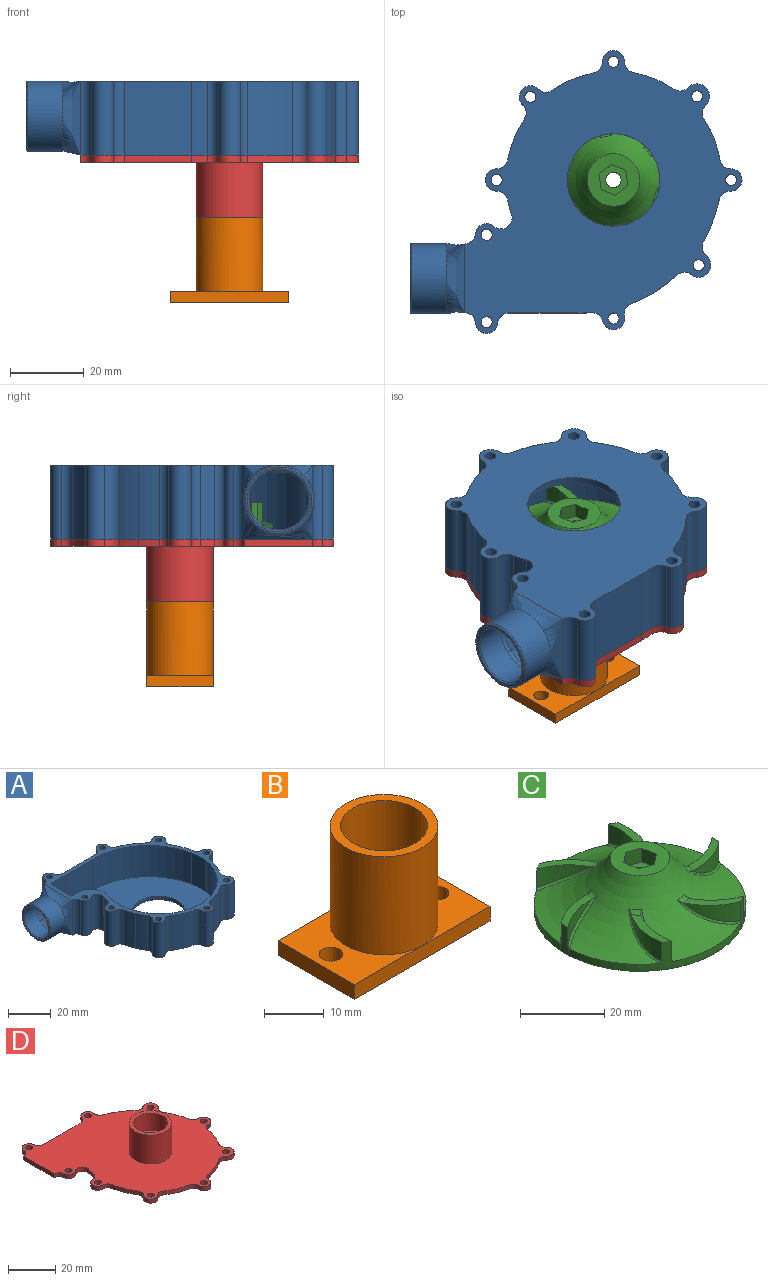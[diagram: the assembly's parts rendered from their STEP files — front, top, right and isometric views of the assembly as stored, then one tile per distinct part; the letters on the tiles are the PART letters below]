
ASSEMBLY  parts=4 mates=3
PART A: 83 faces, bbox 89.8x76.4x20.8 mm
  f0: cylinder r=29.1mm len=20mm, axis (0,0,-1), area 123.2mm2, adj f1,f7,f16,f63
  f1: cylinder r=29.1mm len=20mm, axis (0,0,-1), area 116.2mm2, adj f0,f7,f16,f54
  f2: cylinder r=29.1mm len=20mm, axis (0,0,-1), area 242.2mm2, adj f7,f16,f50,f56
  f3: cylinder r=29.1mm len=20mm, axis (0,0,-1), area 236.9mm2, adj f7,f16,f46,f52
  f4: cylinder r=38.12mm len=20mm, axis (0,0,-1), area 241.8mm2, adj f7,f11,f16,f40
  f5: cylinder r=38.12mm len=20mm, axis (0,0,-1), area 292.6mm2, adj f7,f16,f36,f42
  f6: cylinder r=8.51mm len=18mm, axis (0,0,-1), area 233.2mm2, adj f7,f26,f27,f28,f29,f30
  f7: plane 76.42x75.05mm, normal (0,0,1), area 691.8mm2, adj f0,f1,f2,f3,f4,f5,f6,f8
  f8: cylinder r=29.1mm len=20mm, axis (0,0,-1), area 80mm2, adj f7,f15,f16,f61
  f9: cylinder r=29.1mm len=20mm, axis (0,0,-1), area 235.3mm2, adj f7,f10,f16,f48
  f10: cylinder r=3mm len=20mm, axis (0,0,-1), area 83.6mm2, adj f7,f9,f16,f44
  f11: cylinder r=3mm len=20mm, axis (0,0,-1), area 84.8mm2, adj f4,f7,f16,f44
  f12: cylinder r=38.12mm len=20mm, axis (0,0,-1), area 85.1mm2, adj f7,f13,f16,f38
  f13: plane 20x18.02mm, normal (0,1,0), area 360.4mm2, adj f7,f12,f16,f33
  f14: plane 20x0.02mm, normal (0,-1,0), area 0.4mm2, adj f7,f16,f58,f66
  f15: cylinder r=3mm len=20mm, axis (0,0,-1), area 156mm2, adj f7,f8,f16,f59
  f16: plane 76.42x75.05mm, normal (0,0,-1), area 3092.9mm2, adj f0,f1,f2,f3,f4,f5,f8,f9
  f17: cylinder r=27.1mm len=19.22mm, axis (0,0,-1), area 354mm2, adj f7,f18,f27,f28
  f18: cylinder r=27.1mm len=51.79mm, axis (0,0,-1), area 1258.4mm2, adj f7,f17,f19,f28
  f19: cylinder r=5mm len=18mm, axis (0,0,-1), area 0.8mm2, adj f7,f18,f20,f28
  f20: cylinder r=24.78mm len=18mm, axis (0,0,-1), area 178.9mm2, adj f7,f19,f21,f28
  f21: cylinder r=5mm len=18mm, axis (0,0,-1), area 3.9mm2, adj f7,f20,f22,f28
  f22: cylinder r=36.12mm len=36.86mm, axis (0,0,-1), area 918mm2, adj f7,f21,f23,f28
  f23: plane 18.05x18mm, normal (0,-1,0), area 324.9mm2, adj f7,f22,f24,f28
  f24: plane 18x9.91mm, normal (0.01,-1,0), area 178.4mm2, adj f7,f23,f25,f28
  f25: plane 18x14.36mm, normal (1,0,0), area 29.1mm2, adj f7,f24,f26,f28,f30,f31
  f26: plane 3.82x2mm, normal (-0.08,1,0), area 7.7mm2, adj f6,f7,f25,f30
  f27: cylinder r=5mm len=18mm, axis (0,0,-1), area 7.9mm2, adj f6,f7,f17,f28
  f28: plane 67.53x61.45mm, normal (0,0,1), area 2433mm2, adj f6,f17,f18,f19,f20,f21,f22,f23
  f29: plane 16x9.59mm, normal (0,1,0), area 153.4mm2, adj f6,f28,f30,f73
  f30: plane 14.56x9.59mm, normal (0,0,-1), area 31.9mm2, adj f6,f25,f26,f29,f31,f72
  f31: plane 16x2mm, normal (0,-1,0), area 32mm2, adj f25,f28,f30,f71
  f32: cylinder r=3mm len=20mm, axis (0,0,-1), area 88.8mm2, adj f7,f16,f34,f68
  f33: cylinder r=3mm len=20mm, axis (0,0,-1), area 89.2mm2, adj f7,f13,f16,f34
  f34: cylinder r=3mm len=20mm, axis (0,0,-1), area 179.5mm2, adj f7,f16,f32,f33
  f35: cylinder r=1.5mm len=20mm, axis (0,0,-1), area 188.5mm2, adj f7,f16
  f36: cylinder r=3mm len=20mm, axis (0,0,-1), area 84.2mm2, adj f5,f7,f16,f37
  f37: cylinder r=3mm len=20mm, axis (0,0,-1), area 186mm2, adj f7,f16,f36,f38
  f38: cylinder r=3mm len=20mm, axis (0,0,-1), area 84.2mm2, adj f7,f12,f16,f37
  f39: cylinder r=1.5mm len=20mm, axis (0,0,-1), area 188.5mm2, adj f7,f16
  f40: cylinder r=3mm len=20mm, axis (0,0,-1), area 84.7mm2, adj f4,f7,f16,f41
  f41: cylinder r=3.26mm len=20mm, axis (0,0,-1), area 203.7mm2, adj f7,f16,f40,f42
  f42: cylinder r=3mm len=20mm, axis (0,0,-1), area 84.7mm2, adj f5,f7,f16,f41
  f43: cylinder r=1.5mm len=20mm, axis (0,0,-1), area 188.5mm2, adj f7,f16
  f44: cylinder r=3mm len=20mm, axis (0,0,-1), area 191mm2, adj f7,f10,f11,f16
  f45: cylinder r=1.5mm len=20mm, axis (0,0,-1), area 188.5mm2, adj f7,f16
  f46: cylinder r=3mm len=20mm, axis (0,0,-1), area 83.6mm2, adj f3,f7,f16,f47
  f47: cylinder r=3.38mm len=20mm, axis (0,0,-1), area 215.1mm2, adj f7,f16,f46,f48
  f48: cylinder r=3mm len=20mm, axis (0,0,-1), area 83.6mm2, adj f7,f9,f16,f47
  f49: cylinder r=1.5mm len=20mm, axis (0,0,-1), area 188.5mm2, adj f7,f16
  f50: cylinder r=3mm len=20mm, axis (0,0,-1), area 83.6mm2, adj f2,f7,f16,f51
  f51: cylinder r=3mm len=20mm, axis (0,0,-1), area 189.8mm2, adj f7,f16,f50,f52
  f52: cylinder r=3mm len=20mm, axis (0,0,-1), area 83.6mm2, adj f3,f7,f16,f51
  f53: cylinder r=1.5mm len=20mm, axis (0,0,-1), area 188.5mm2, adj f7,f16
  f54: cylinder r=3mm len=20mm, axis (0,0,-1), area 83.6mm2, adj f1,f7,f16,f55
  f55: cylinder r=3mm len=20mm, axis (0,0,-1), area 189.8mm2, adj f7,f16,f54,f56
  f56: cylinder r=3mm len=20mm, axis (0,0,-1), area 83.6mm2, adj f2,f7,f16,f55
  f57: cylinder r=1.5mm len=20mm, axis (0,0,-1), area 188.5mm2, adj f7,f16
  f58: cylinder r=3mm len=20mm, axis (0,0,-1), area 89.2mm2, adj f7,f14,f16,f59
  f59: cylinder r=3mm len=20mm, axis (0,0,-1), area 131.5mm2, adj f7,f15,f16,f58
  f60: cylinder r=1.5mm len=20mm, axis (0,0,-1), area 188.5mm2, adj f7,f16
  f61: cylinder r=3mm len=20mm, axis (0,0,-1), area 83.6mm2, adj f7,f8,f16,f62
  f62: cylinder r=3mm len=20mm, axis (0,0,-1), area 189.8mm2, adj f7,f16,f61,f63
  f63: cylinder r=3mm len=20mm, axis (0,0,-1), area 83.6mm2, adj f0,f7,f16,f62
  f64: cylinder r=1.5mm len=20mm, axis (0,0,-1), area 188.5mm2, adj f7,f16
  f65: cylinder r=12.5mm len=25mm, axis (0,0,-1), area 157.1mm2, adj f16,f28
  f66: bspline ~20x4.7mm, area 84.7mm2, adj f14,f67,f69,f74
  f67: bspline ~18.52x4.79mm, area 86.6mm2, adj f7,f66,f68,f74
  f68: bspline ~20x4.79mm, area 85.6mm2, adj f32,f67,f69,f74
  f69: bspline ~18.52x4.79mm, area 81.8mm2, adj f16,f66,f68,f74
  f70: bspline ~14.52x4.78mm, area 65.1mm2, adj f28,f71,f73,f79
  f71: bspline ~16x4.78mm, area 69.3mm2, adj f31,f70,f72,f80
  f72: bspline ~14.52x4.78mm, area 66.7mm2, adj f30,f71,f73,f78
  f73: bspline ~16x4.71mm, area 68.3mm2, adj f29,f70,f72,f77
  f74: cylinder r=9.5mm len=19mm, axis (1,0,0), area 567.1mm2, adj f66,f67,f68,f69,f82
  f75: plane 18x18mm, normal (-1,0,0), area 27.5mm2, adj f81,f82
  f76: cylinder r=8mm len=16mm, axis (-1,0,0), area 399mm2, adj f77,f78,f79,f80,f81
  f77: bspline ~12.11x2.96mm, area 20.1mm2, adj f73,f76,f78,f79
  f78: bspline ~12.11x2.96mm, area 20.2mm2, adj f72,f76,f77,f80
  f79: bspline ~12.11x2.96mm, area 20.2mm2, adj f70,f76,f77,f80
  f80: bspline ~12.11x2.96mm, area 20.2mm2, adj f71,f76,f78,f79
  f81: torus R=8.5mm, axis (1,0,0), area 40.4mm2, adj f75,f76
  f82: torus R=9mm, axis (1,0,0), area 46mm2, adj f74,f75
PART B: 12 faces, bbox 32x18x23 mm
  f0: cylinder r=7.25mm len=23mm, axis (0,0,-1), area 1047.7mm2, adj f2,f9
  f1: cylinder r=9mm len=20mm, axis (0,0,-1), area 1131mm2, adj f2,f3,f6
  f2: plane 18x18mm, normal (0,0,1), area 89.3mm2, adj f0,f1
  f3: plane 18x16mm, normal (0,0,1), area 148.2mm2, adj f1,f5,f7,f8,f11
  f4: plane 18x3mm, normal (-1,0,0), area 54mm2, adj f6,f7,f8,f9
  f5: plane 18x3mm, normal (1,0,0), area 54mm2, adj f3,f7,f8,f9
  f6: plane 18x16mm, normal (0,0,1), area 148.2mm2, adj f1,f4,f7,f8,f10
  f7: plane 32x3mm, normal (0,1,0), area 96mm2, adj f3,f4,f5,f6,f9
  f8: plane 32x3mm, normal (0,-1,0), area 96mm2, adj f3,f4,f5,f6,f9
  f9: plane 32x18mm, normal (0,0,-1), area 385.7mm2, adj f0,f4,f5,f7,f8,f10,f11
  f10: cylinder r=2mm len=4mm, axis (0,0,-1), area 37.7mm2, adj f6,f9
  f11: cylinder r=2mm len=4mm, axis (0,0,-1), area 37.7mm2, adj f3,f9
PART C: 48 faces, bbox 61.1x61.1x26.7 mm
  f0: cylinder r=2.1mm len=11mm, axis (0,0,-1), area 145.1mm2, adj f3,f29
  f1: torus R=29.21mm, axis (0,0,-1), area 1865.6mm2, adj f2,f4,f30,f31,f32,f33,f34,f35
  f2: plane 14.2x14.2mm, normal (0,0,1), area 112.2mm2, adj f1,f23,f24,f25,f26,f27,f28
  f3: plane 50.2x50.2mm, normal (0,0,-1), area 1965.4mm2, adj f0,f4
  f4: cylinder r=25.1mm len=50.2mm, axis (0,0,-1), area 400.2mm2, adj f1,f3,f5,f6,f7,f8,f9,f10
  f5: cylinder r=18mm len=12.05mm, axis (0,0,-1), area 35.5mm2, adj f4,f7,f39
  f6: cylinder r=18mm len=13.06mm, axis (0,0,-1), area 49.9mm2, adj f4,f7,f38,f46
  f7: plane 12.88x6.41mm, normal (0,0,1), area 27.6mm2, adj f4,f5,f6,f39,f46
  f8: plane 14.32x4.63mm, normal (0,0,1), area 27.6mm2, adj f4,f9,f10,f37,f45
  f9: cylinder r=18mm len=13.33mm, axis (0,0,-1), area 49.9mm2, adj f4,f8,f36,f45
  f10: cylinder r=18mm len=12.56mm, axis (0,0,-1), area 35.5mm2, adj f4,f8,f37
  f11: plane 12.88x6.41mm, normal (0,0,1), area 27.6mm2, adj f4,f12,f13,f33,f43
  f12: cylinder r=18mm len=12.05mm, axis (0,0,-1), area 35.5mm2, adj f4,f11,f33
  f13: cylinder r=18mm len=13.06mm, axis (0,0,-1), area 49.9mm2, adj f4,f11,f32,f43
  f14: cylinder r=18mm len=13.33mm, axis (0,0,-1), area 49.9mm2, adj f4,f16,f30,f42
  f15: cylinder r=18mm len=12.56mm, axis (0,0,-1), area 35.5mm2, adj f4,f16,f31
  f16: plane 14.32x4.63mm, normal (0,0,1), area 27.6mm2, adj f4,f14,f15,f31,f42
  f17: cylinder r=18mm len=10.03mm, axis (0,0,-1), area 49.9mm2, adj f4,f19,f34,f44
  f18: cylinder r=18mm len=9.7mm, axis (0,0,-1), area 35.5mm2, adj f4,f19,f35
  f19: plane 11.94x9.52mm, normal (0,0,1), area 27.6mm2, adj f4,f17,f18,f35,f44
  f20: cylinder r=18mm len=9.7mm, axis (0,0,-1), area 35.5mm2, adj f4,f22,f40
  f21: cylinder r=18mm len=10.03mm, axis (0,0,-1), area 49.9mm2, adj f4,f22,f41,f47
  f22: plane 11.94x9.52mm, normal (0,0,1), area 27.6mm2, adj f4,f20,f21,f40,f47
  f23: plane 4x3.93mm, normal (0.36,0.93,0), area 16.9mm2, adj f2,f24,f28,f29
  f24: plane 4x3.28mm, normal (-0.63,0.78,0), area 16.9mm2, adj f2,f23,f25,f29
  f25: plane 4.16x4mm, normal (-0.99,-0.15,0), area 16.9mm2, adj f2,f24,f26,f29
  f26: plane 4x3.93mm, normal (-0.36,-0.93,0), area 16.9mm2, adj f2,f25,f27,f29
  f27: plane 4x3.28mm, normal (0.63,-0.78,0), area 16.9mm2, adj f2,f26,f28,f29
  f28: plane 4.16x4mm, normal (0.99,0.15,0), area 16.9mm2, adj f2,f23,f27,f29
  f29: plane 8.33x7.86mm, normal (0,0,1), area 32.3mm2, adj f0,f23,f24,f25,f26,f27,f28
  f30: bspline ~17.28x8.18mm, area 11mm2, adj f1,f4,f14,f42
  f31: bspline ~16.64x8.2mm, area 13.1mm2, adj f1,f4,f15,f16,f42
  f32: bspline ~16.34x8.08mm, area 11mm2, adj f1,f4,f13,f43
  f33: bspline ~16.1x8.2mm, area 13.1mm2, adj f1,f4,f11,f12,f43
  f34: bspline ~12.58x12.41mm, area 11mm2, adj f1,f4,f17,f44
  f35: bspline ~12.7x10.93mm, area 13.1mm2, adj f1,f4,f18,f19,f44
  f36: bspline ~17.28x8.18mm, area 11mm2, adj f1,f4,f9,f45
  f37: bspline ~16.64x8.2mm, area 13.1mm2, adj f1,f4,f8,f10,f45
  f38: bspline ~16.34x8.08mm, area 11mm2, adj f1,f4,f6,f46
  f39: bspline ~16.1x8.2mm, area 13.1mm2, adj f1,f4,f5,f7,f46
  f40: bspline ~12.7x10.93mm, area 13.1mm2, adj f1,f4,f20,f22,f47
  f41: bspline ~12.58x12.41mm, area 11mm2, adj f1,f4,f21,f47
  f42: torus R=13.36mm, axis (0,0,1), area 4mm2, adj f1,f14,f16,f30,f31
  f43: torus R=13.36mm, axis (0,0,1), area 4mm2, adj f1,f11,f13,f32,f33
  f44: torus R=13.36mm, axis (0,0,1), area 4mm2, adj f1,f17,f19,f34,f35
  f45: torus R=13.36mm, axis (0,0,1), area 4mm2, adj f1,f8,f9,f36,f37
  f46: torus R=13.36mm, axis (0,0,1), area 4mm2, adj f1,f6,f7,f38,f39
  f47: torus R=13.36mm, axis (0,0,1), area 4mm2, adj f1,f21,f22,f40,f41
PART D: 62 faces, bbox 75.1x76.4x17 mm
  f0: cylinder r=2.25mm len=4.5mm, axis (0,0,1), area 28.3mm2, adj f50,f61
  f1: cylinder r=29.1mm len=5.89mm, axis (0,0,-1), area 12.3mm2, adj f2,f47,f49,f50
  f2: cylinder r=29.1mm len=5.13mm, axis (0,0,-1), area 11.6mm2, adj f1,f3,f49,f50
  f3: cylinder r=3mm len=3.83mm, axis (0,0,-1), area 8.4mm2, adj f2,f4,f49,f50
  f4: cylinder r=3mm len=5.17mm, axis (0,0,-1), area 19mm2, adj f3,f5,f49,f50
  f5: cylinder r=3mm len=3.84mm, axis (0,0,-1), area 8.4mm2, adj f4,f6,f49,f50
  f6: cylinder r=29.1mm len=11.07mm, axis (0,0,-1), area 24.2mm2, adj f5,f7,f49,f50
  f7: cylinder r=3mm len=2.99mm, axis (0,0,-1), area 8.4mm2, adj f6,f8,f49,f50
  f8: cylinder r=3mm len=6mm, axis (0,0,-1), area 19mm2, adj f7,f9,f49,f50
  f9: cylinder r=3mm len=2.97mm, axis (0,0,-1), area 8.4mm2, adj f8,f10,f49,f50
  f10: cylinder r=29.1mm len=10.9mm, axis (0,0,-1), area 23.7mm2, adj f9,f11,f49,f50
  f11: cylinder r=3mm len=3.83mm, axis (0,0,-1), area 8.4mm2, adj f10,f12,f49,f50
  f12: cylinder r=3.38mm len=5.83mm, axis (0,0,-1), area 21.5mm2, adj f11,f13,f49,f50
  f13: cylinder r=3mm len=3.82mm, axis (0,0,-1), area 8.4mm2, adj f12,f14,f49,f50
  f14: cylinder r=29.1mm len=10.86mm, axis (0,0,-1), area 23.5mm2, adj f13,f15,f49,f50
  f15: cylinder r=3mm len=2.95mm, axis (0,0,-1), area 8.4mm2, adj f14,f16,f49,f50
  f16: cylinder r=3mm len=6mm, axis (0,0,-1), area 19.1mm2, adj f15,f17,f49,f50
  f17: cylinder r=3mm len=3.07mm, axis (0,0,-1), area 8.5mm2, adj f16,f18,f49,f50
  f18: cylinder r=38.12mm len=11.28mm, axis (0,0,-1), area 24.2mm2, adj f17,f19,f49,f50
  f19: cylinder r=3mm len=3.82mm, axis (0,0,-1), area 8.5mm2, adj f18,f20,f49,f50
  f20: cylinder r=3.26mm len=5.8mm, axis (0,0,-1), area 20.4mm2, adj f19,f21,f49,f50
  f21: cylinder r=3mm len=3.89mm, axis (0,0,-1), area 8.5mm2, adj f20,f22,f49,f50
  f22: cylinder r=38.12mm len=12.34mm, axis (0,0,-1), area 29.3mm2, adj f21,f23,f49,f50
  f23: cylinder r=3mm len=3.39mm, axis (0,0,-1), area 8.4mm2, adj f22,f24,f49,f50
  f24: cylinder r=3mm len=5.91mm, axis (0,0,-1), area 18.6mm2, adj f23,f25,f49,f50
  f25: cylinder r=3mm len=3.13mm, axis (0,0,-1), area 8.4mm2, adj f24,f26,f49,f50
  f26: cylinder r=38.12mm len=4.25mm, axis (0,0,-1), area 8.5mm2, adj f25,f27,f49,f50
  f27: plane 18.02x2mm, normal (0,1,0), area 36mm2, adj f26,f28,f49,f50
  f28: cylinder r=3mm len=2.99mm, axis (0,0,-1), area 8.9mm2, adj f27,f29,f49,f50
  f29: cylinder r=3mm len=5.98mm, axis (0,0,-1), area 18mm2, adj f28,f30,f49,f50
  f30: cylinder r=3mm len=2.92mm, axis (0,0,-1), area 8.9mm2, adj f29,f31,f49,f50
  f31: plane 18.52x2mm, normal (-1,0,0), area 37mm2, adj f30,f32,f49,f50
  f32: plane 2x0.02mm, normal (0,-1,0), area 0mm2, adj f31,f33,f49,f50
  f33: cylinder r=3mm len=2.99mm, axis (0,0,-1), area 8.9mm2, adj f32,f34,f49,f50
  f34: cylinder r=3mm len=4.93mm, axis (0,0,-1), area 13.1mm2, adj f33,f35,f49,f50
  f35: cylinder r=3mm len=4.94mm, axis (0,0,-1), area 15.6mm2, adj f34,f36,f49,f50
  f36: cylinder r=29.1mm len=3.87mm, axis (0,0,-1), area 8mm2, adj f35,f37,f49,f50
  f37: cylinder r=3mm len=2.98mm, axis (0,0,-1), area 8.4mm2, adj f36,f38,f49,f50
  f38: cylinder r=3mm len=6mm, axis (0,0,-1), area 19mm2, adj f37,f47,f49,f50
  f39: cylinder r=1.5mm len=3mm, axis (0,0,-1), area 18.8mm2, adj f49,f50
  f40: cylinder r=1.5mm len=3mm, axis (0,0,-1), area 18.8mm2, adj f49,f50
  f41: cylinder r=1.5mm len=3mm, axis (0,0,-1), area 18.8mm2, adj f49,f50
  f42: cylinder r=1.5mm len=3mm, axis (0,0,-1), area 18.8mm2, adj f49,f50
  f43: cylinder r=1.5mm len=3mm, axis (0,0,-1), area 18.8mm2, adj f49,f50
  f44: cylinder r=1.5mm len=3mm, axis (0,0,-1), area 18.8mm2, adj f49,f50
  f45: cylinder r=1.5mm len=3mm, axis (0,0,-1), area 18.8mm2, adj f49,f50
  f46: cylinder r=1.5mm len=3mm, axis (0,0,-1), area 18.8mm2, adj f49,f50
  f47: cylinder r=3mm len=2.98mm, axis (0,0,-1), area 8.4mm2, adj f1,f38,f49,f50
  f48: cylinder r=1.5mm len=3mm, axis (0,0,-1), area 18.8mm2, adj f49,f50
  f49: plane 76.42x75.05mm, normal (0,0,1), area 3329.3mm2, adj f1,f2,f3,f4,f5,f6,f7,f8
  f50: plane 76.42x75.05mm, normal (0,0,-1), area 3567.9mm2, adj f0,f1,f2,f3,f4,f5,f6,f7
  f51: cylinder r=7.25mm len=14.5mm, axis (0,0,-1), area 410mm2, adj f53,f54
  f52: cylinder r=9mm len=18mm, axis (0,0,-1), area 848.2mm2, adj f49,f53
  f53: plane 18x18mm, normal (0,0,1), area 89.3mm2, adj f51,f52
  f54: plane 14.5x14.5mm, normal (0,0,1), area 120.2mm2, adj f51,f55,f56,f57,f58,f59,f60
  f55: plane 6x3.62mm, normal (0.49,0.87,0), area 24.9mm2, adj f54,f56,f60,f61
  f56: plane 6x3.58mm, normal (-0.51,0.86,0), area 24.9mm2, adj f54,f55,f57,f61
  f57: plane 6x4.16mm, normal (-1,-0.01,0), area 24.9mm2, adj f54,f56,f58,f61
  f58: plane 6x3.62mm, normal (-0.49,-0.87,0), area 24.9mm2, adj f54,f57,f59,f61
  f59: plane 6x3.58mm, normal (0.51,-0.86,0), area 24.9mm2, adj f54,f58,f60,f61
  f60: plane 6x4.16mm, normal (1,0.01,0), area 24.9mm2, adj f54,f55,f59,f61
  f61: plane 8.31x7.23mm, normal (0,0,1), area 29mm2, adj f0,f55,f56,f57,f58,f59,f60
PLACE A rot(axis=(1,0,0),180deg) t=(-3.18,10.79,29.44)mm
PLACE B t=(-3.18,10.79,-30.56)mm
PLACE C t=(-3.18,10.79,27.57)mm
PLACE D rot(axis=(1,0,0),180deg) t=(-3.18,10.79,9.44)mm
MATE revolute C.f0 <-> A.f65  axis (0,0,1) through (-3.18,10.79,26.44)mm
MATE fastened B.f1 <-> D.f51  axis (0,0,1) through (-3.18,10.79,-7.56)mm
MATE fastened D.f50 <-> A.f7  axis (0,0,1) through (-43.44,-15.81,9.44)mm
